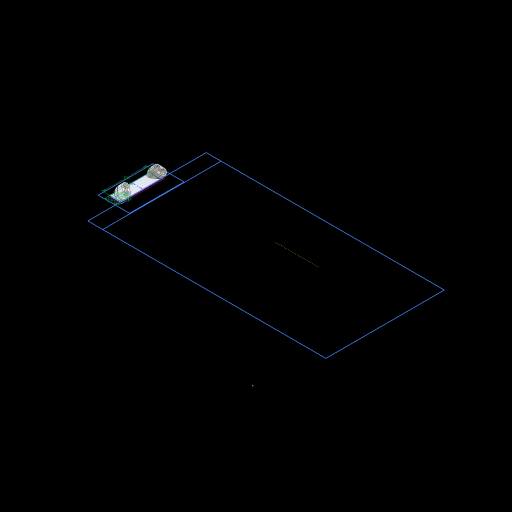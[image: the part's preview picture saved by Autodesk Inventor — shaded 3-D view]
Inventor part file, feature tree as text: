
AUTODESK INVENTOR PART (.ipt)
format: ipt  version: 2023 (Build 270158000, 158)  size: 467,968 bytes
history: native  units: mm
features: extrude x12, sketch x11, plane x3, revolve x2, chamfer x2, sweep x1, fillet x1, mirror x1
ambient origin geometry x8: Origin, YZ Plane, XZ Plane, XY Plane, X Axis, Y Axis, Z Axis, Center Point
bodies: Solid1 (feature_tree)
feature tree (33):
  sketch  "Sketch1"  dims[d0=100.0mm d1=25.0mm d2=7.5mm d3=7.5mm d4=60.0deg d5=15.0mm d6=11.0mm d7=11.0mm d8=15.0mm d11=135.0deg]
  plane  "Work Plane1"
  sweep  "Sweep1"
  extrude  "Extrusion1"  Depth=4.0mm TaperAngle=0.0deg
  fillet  "Fillet1"  Radius=3.0mm
  revolve  "Revolution1"  Angle=45.0deg
  sketch  "Sketch6"  dims[d31=10.0mm d32=45.0deg]
  extrude  "Extrusion4"  TaperAngle=45.0deg  [1 undecoded]
  extrude  "Extrusion5"  Depth=10.0mm
  sketch  "Sketch7"  dims[d33=10.0mm d34=10.0mm]
  extrude  "Extrusion6"  Depth=10.0mm
  extrude  "Extrusion7"  Depth=15.0mm
  mirror  "Mirror4"
  plane  "Work Plane9"
  extrude  "Extrusion8"  Depth=5.5mm
  revolve  "Revolution2"  [1 undecoded]
  extrude  "Extrusion9"  Depth=6.5mm
  sketch  "Sketch19"  dims[d60=5.5mm d61=5.5mm]
  extrude  "Extrusion10"  Depth=10.0mm TaperAngle=0.0deg
  extrude  "Extrusion11"  Depth=10.0mm TaperAngle=0.0deg
  extrude  "Extrusion12"  Depth=7.5mm
  sketch  "Sketch21"  dims[d65=2.0mm d66=6.5mm]
  extrude  "Extrusion13"  TaperAngle=90.0deg  [1 undecoded]
  extrude  "Extrusion14"  Depth=7.5mm
  chamfer  "Chamfer3"  Distance=5.5mm
  chamfer  "Chamfer4"  Distance=5.5mm
  plane  "Work Plane13"
  sketch  "Sketch23"  dims[d67=6.5mm d68=12.5mm d69=0.0mm d70=325.0mm d71=0.0mm d72=7.5mm d73=90.0deg d74=7.5mm d75=5.5mm d76=5.5mm d77=15.0mm d78=11.0mm d79=11.0mm d80=2.0mm d81=6.5mm d82=6.5mm d83=10.0mm d84=0.0mm d93=10.0mm d94=0.0mm d115=20.0mm d116=0.0mm d131=8.726646mm d132=300.0mm d133=0.0mm d134=15.0mm d135=300.0mm d136=0.0mm d137=11.0mm d138=11.0mm d139=2.0mm d140=6.5mm d141=6.5mm d142=10.0mm d143=0.0mm d144=40.0mm d145=0.0mm d146=25.0mm d147=100.0mm d150=15.0mm d151=5.5mm d152=2.0mm d153=0.0mm d154=10.0mm d155=0.0mm d156=2.0mm d157=4.0mm d158=45.0deg d159=2.0mm d160=4.0mm d161=45.0deg d174=10.0mm d175=0.5mm d176=0.872665mm d177=0.5mm d178=0.872665mm d192=1.0mm d193=1.0mm d194=1.0mm d195=0.15mm d196=0.25mm d197=0.375mm d198=14.3117mm d199=0.75mm d200=20.594885mm d201=0.0625mm d202=0.75mm d203=0.375mm d227=0.5mm d228=0.872665mm d229=0.5mm d230=0.872665mm d255=0.5mm d256=0.872665mm d257=0.5mm d258=0.872665mm]
  sketch  "Sketch3"  dims[d12=0.0mm d13=0.0mm d14=4.0mm d15=0.0mm d28=3.0mm]
  sketch  "Sketch5"  dims[d29=11.389087mm d30=45.0deg]
  sketch  "Sketch14"  dims[d35=45.0deg d37=10.0mm]
  sketch  "Sketch15"  dims[d38=0.977384mm d57=15.0mm]
  sketch  "Sketch20"  dims[d63=11.0mm d64=11.0mm]
note: 3 required parameter values undecoded (feature->parameter linkage not recoverable at this tier; creation-order binding heuristic only, values carry confidence <= 0.55)